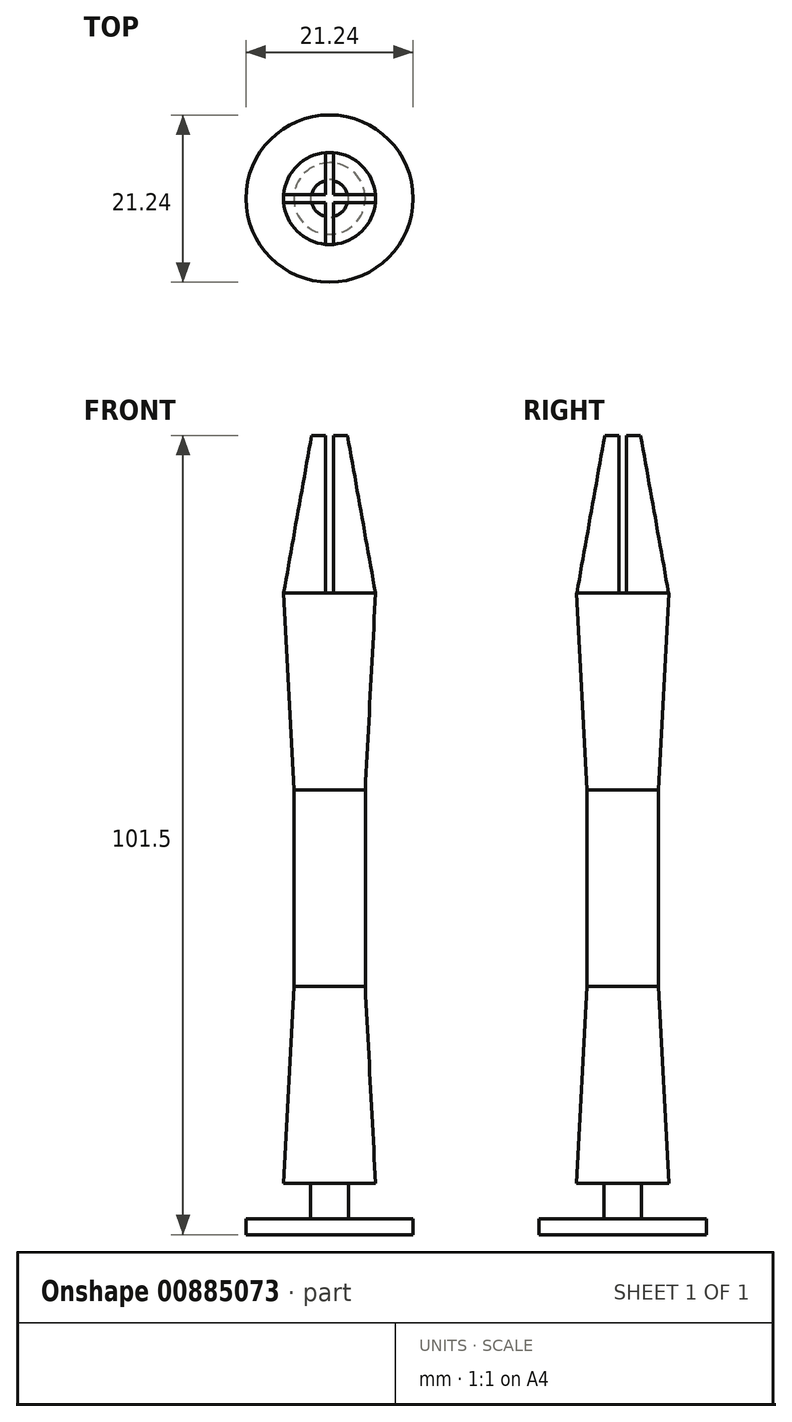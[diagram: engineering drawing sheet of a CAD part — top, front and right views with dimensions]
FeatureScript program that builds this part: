
annotation { "Feature Type Name" : "Feature", "Feature Type Description" : "" }
export const myFeature = defineFeature(function(context is Context, id is Id, definition is map)
    precondition{}
    {
        {
            var Q0;
            Q0=qCreatedBy(makeId("Top.planeOp"),FACE);
            var sketch = newSketch(context, id + "F0", { "sketchPlane" : qUnion([Q0])});
            skCircle(sketch, "E0", {"center": v(0, 0) * mm, "radius": 5.85 * mm});
            skSolve(sketch);
        }
        {
            var Q0;
            Q0=makeQuery(id+"F0.imprint","IMPRINT",FACE,{"disambiguationData":[TD([[makeQuery(id+"F0.imprint","IMPRINT",EDGE,{"derivedFrom":sQuery(id+"F0.wireOp",EDGE,"E0")}),1.0]])]});
            var Q1;
            Q1=sQuery(id+"F0.wireOp",EDGE,"E0");
            extrude(context, id + "F1", {"entities" : qUnion([Q0]), "surfaceEntities" : qUnion([Q1]), "depth" : 25 * mm, "offsetDistance" : 25 * mm, "hasDraft" : true, "draftAngle" : 3 * degree, "draftPullDirection" : true});
        }
        {
            var Q0;
            Q0=makeQuery(id+"F1.opExtrude","CAP_FACE",FACE,{"disambiguationData":[OSD([sQuery(id+"F0.wireOp",EDGE,"E0")])],"isStart":false});
            extrude(context, id + "F2", {"entities" : qUnion([Q0]), "operationType" : NewBodyOperationType.ADD, "depth" : 25 * mm, "offsetDistance" : 25 * mm});
        }
        {
            var Q0;
            Q0=makeQuery(id+"F2.opExtrude","CAP_FACE",FACE,{"disambiguationData":[OSD([sQuery(id+"F0.wireOp",EDGE,"E0")])],"isStart":false});
            extrude(context, id + "F3", {"entities" : qUnion([Q0]), "operationType" : NewBodyOperationType.ADD, "depth" : 25 * mm, "offsetDistance" : 25 * mm, "hasDraft" : true, "draftAngle" : 3 * degree});
        }
        {
            var Q0;
            Q0=makeQuery(id+"F1.opExtrude","CAP_FACE",FACE,{"disambiguationData":[OSD([sQuery(id+"F0.wireOp",EDGE,"E0")])],"isStart":true});
            var sketch = newSketch(context, id + "F4", { "sketchPlane" : qUnion([Q0])});
            skCircle(sketch, "E1", {"center": v(0, 0) * mm, "radius": 2.4 * mm});
            skSolve(sketch);
        }
        {
            var Q0;
            Q0=makeQuery(id+"F4.imprint","IMPRINT",FACE,{"disambiguationData":[TD([[makeQuery(id+"F4.imprint","IMPRINT",EDGE,{"derivedFrom":sQuery(id+"F4.wireOp",EDGE,"E1")}),1.0]])]});
            extrude(context, id + "F5", {"entities" : qUnion([Q0]), "operationType" : NewBodyOperationType.ADD, "depth" : 4.5 * mm, "offsetDistance" : 25 * mm});
        }
        {
            var Q0;
            Q0=makeQuery(id+"F3.opExtrude","CAP_FACE",FACE,{"disambiguationData":[OSD([sQuery(id+"F0.wireOp",EDGE,"E0")])],"isStart":false});
            extrude(context, id + "F6", {"entities" : qUnion([Q0]), "operationType" : NewBodyOperationType.ADD, "depth" : 20 * mm, "offsetDistance" : 25 * mm, "hasDraft" : true, "draftAngle" : 10 * degree, "draftPullDirection" : true});
        }
        {
            var Q0;
            Q0=makeQuery(id+"F6.opExtrude","CAP_FACE",FACE,{"disambiguationData":[OSD([sQuery(id+"F0.wireOp",EDGE,"E0")])],"isStart":false});
            var sketch = newSketch(context, id + "F7", { "sketchPlane" : qUnion([Q0])});
            skLineSegment(sketch, "E2.bottom", {"start": v(-10.12, -0.5) * mm, "end": v(10.12, -0.5) * mm});
            skLineSegment(sketch, "E2.top", {"start": v(-10.12, 0.5) * mm, "end": v(10.12, 0.5) * mm});
            skLineSegment(sketch, "E2.left", {"start": v(-10.12, -0.5) * mm, "end": v(-10.12, 0.5) * mm});
            skLineSegment(sketch, "E2.right", {"start": v(10.12, -0.5) * mm, "end": v(10.12, 0.5) * mm});
            skPoint(sketch, "E2.middle", {"position": v(0, 0) * mm});
            skLineSegment(sketch, "E3.bottom", {"start": v(0.5, 11.68) * mm, "end": v(-0.5, 11.68) * mm});
            skLineSegment(sketch, "E3.top", {"start": v(0.5, -11.68) * mm, "end": v(-0.5, -11.68) * mm});
            skLineSegment(sketch, "E3.left", {"start": v(0.5, 11.68) * mm, "end": v(0.5, -11.68) * mm});
            skLineSegment(sketch, "E3.right", {"start": v(-0.5, 11.68) * mm, "end": v(-0.5, -11.68) * mm});
            skSolve(sketch);
        }
        {
            var Q0;
            {var subQ0=sQuery(id+"F7.wireOp",EDGE,"E3.right");var subQ1=sQuery(id+"F7.wireOp",EDGE,"E2.top");var subQ2=makeQuery(id+"F7.imprint","INTERSECT",VERTEX,{"derivedFrom":[subQ1,subQ0]});Q0=makeQuery(id+"F7.imprint","IMPRINT",FACE,{"disambiguationData":[TD([[makeQuery(id+"F7.imprint","IMPRINT",EDGE,{"disambiguationData":[TD([[subQ2,-1.0]])],"derivedFrom":subQ1}),1.0]])]});}
            var Q1;
            {var subQ0=sQuery(id+"F7.wireOp",EDGE,"E3.right");var subQ1=sQuery(id+"F7.wireOp",EDGE,"E2.bottom");var subQ2=makeQuery(id+"F7.imprint","INTERSECT",VERTEX,{"derivedFrom":[subQ1,subQ0]});Q1=makeQuery(id+"F7.imprint","IMPRINT",FACE,{"disambiguationData":[TD([[makeQuery(id+"F7.imprint","IMPRINT",EDGE,{"disambiguationData":[TD([[subQ2,1.0]])],"derivedFrom":subQ1}),1.0]])]});}
            var Q2;
            {var subQ0=sQuery(id+"F7.wireOp",EDGE,"E3.right");var subQ1=sQuery(id+"F7.wireOp",EDGE,"E2.bottom");var subQ2=makeQuery(id+"F7.imprint","INTERSECT",VERTEX,{"derivedFrom":[subQ1,subQ0]});Q2=makeQuery(id+"F7.imprint","IMPRINT",FACE,{"disambiguationData":[TD([[makeQuery(id+"F7.imprint","IMPRINT",EDGE,{"disambiguationData":[TD([[subQ2,-1.0]])],"derivedFrom":subQ1}),-1.0]])]});}
            var Q3;
            {var subQ0=sQuery(id+"F7.wireOp",EDGE,"E3.left");var subQ1=sQuery(id+"F7.wireOp",EDGE,"E2.bottom");var subQ2=makeQuery(id+"F7.imprint","INTERSECT",VERTEX,{"derivedFrom":[subQ1,subQ0]});Q3=makeQuery(id+"F7.imprint","IMPRINT",FACE,{"disambiguationData":[TD([[makeQuery(id+"F7.imprint","IMPRINT",EDGE,{"disambiguationData":[TD([[subQ2,-1.0]])],"derivedFrom":subQ1}),1.0]])]});}
            var Q4;
            {var subQ0=sQuery(id+"F7.wireOp",EDGE,"E3.right");var subQ1=sQuery(id+"F7.wireOp",EDGE,"E2.bottom");var subQ2=makeQuery(id+"F7.imprint","INTERSECT",VERTEX,{"derivedFrom":[subQ1,subQ0]});Q4=makeQuery(id+"F7.imprint","IMPRINT",FACE,{"disambiguationData":[TD([[makeQuery(id+"F7.imprint","IMPRINT",EDGE,{"disambiguationData":[TD([[subQ2,-1.0]])],"derivedFrom":subQ1}),1.0]])]});}
            var Q5;
            {var subQ0=sQuery(id+"F7.wireOp",EDGE,"E2.left");Q5=makeQuery(id+"F7.imprint","IMPRINT",FACE,{"disambiguationData":[TD([[makeQuery(id+"F7.imprint","IMPRINT",EDGE,{"derivedFrom":subQ0}),-1.0]])]});}
            var Q6;
            {var subQ0=sQuery(id+"F7.wireOp",EDGE,"E3.top");Q6=makeQuery(id+"F7.imprint","IMPRINT",FACE,{"disambiguationData":[TD([[makeQuery(id+"F7.imprint","IMPRINT",EDGE,{"derivedFrom":subQ0}),-1.0]])]});}
            var Q7;
            {var subQ0=sQuery(id+"F7.wireOp",EDGE,"E2.right");Q7=makeQuery(id+"F7.imprint","IMPRINT",FACE,{"disambiguationData":[TD([[makeQuery(id+"F7.imprint","IMPRINT",EDGE,{"derivedFrom":subQ0}),1.0]])]});}
            var Q8;
            {var subQ0=sQuery(id+"F7.wireOp",EDGE,"E3.bottom");Q8=makeQuery(id+"F7.imprint","IMPRINT",FACE,{"disambiguationData":[TD([[makeQuery(id+"F7.imprint","IMPRINT",EDGE,{"derivedFrom":subQ0}),1.0]])]});}
            extrude(context, id + "F8", {"entities" : qUnion([Q0, Q1, Q2, Q3, Q4, Q5, Q6, Q7, Q8]), "operationType" : NewBodyOperationType.REMOVE, "oppositeDirection" : true, "depth" : 20 * mm, "offsetDistance" : 25 * mm});
        }
        {
            var Q0;
            Q0=makeQuery(id+"F5.opExtrude","CAP_FACE",FACE,{"disambiguationData":[OSD([sQuery(id+"F4.wireOp",EDGE,"E1")])],"isStart":false});
            var sketch = newSketch(context, id + "F9", { "sketchPlane" : qUnion([Q0])});
            skCircle(sketch, "E4", {"center": v(0, 0) * mm, "radius": 10.62 * mm});
            skSolve(sketch);
        }
        {
            var Q0;
            Q0=makeQuery(id+"F9.imprint","IMPRINT",FACE,{"disambiguationData":[TD([[makeQuery(id+"F9.imprint","IMPRINT",EDGE,{"derivedFrom":sQuery(id+"F9.wireOp",EDGE,"E4")}),1.0]])]});
            var Q1;
            Q1=makeQuery(id+"F9.imprint","IMPRINT",FACE,{"disambiguationData":[TD([[makeQuery(id+"F9.imprint","IMPRINT",EDGE,{"derivedFrom":makeQuery(id+"F5.opExtrude","CAP_EDGE",EDGE,{"disambiguationData":[OSD([sQuery(id+"F4.wireOp",EDGE,"E1")])],"isStart":false})}),1.0]])]});
            extrude(context, id + "F10", {"entities" : qUnion([Q0, Q1]), "depth" : 2 * mm, "offsetDistance" : 25 * mm});
        }
    });
